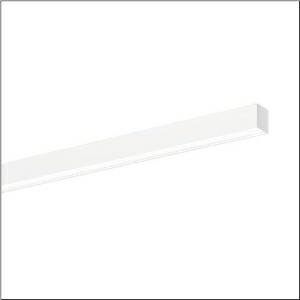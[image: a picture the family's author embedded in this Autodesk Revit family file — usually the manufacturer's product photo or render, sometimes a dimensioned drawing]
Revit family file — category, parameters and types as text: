
# Revit family: silica_21_51mx23dc4awb
name_source: partatom
category: Lighting Fixtures
units: mm (PartAtom-declared; Revit-internal decimal feet)

## family parameters
Cut with Voids When Loaded = No
Host = Face
Light Source = No
Part Type = Normal
Room Calculation Point = No
Round Connector Dimension = Use Diameter
Shared = No

## types (1)
- --- (1 x LED, 8200 lm, 58.2 W, 4000K)
    Apparent Load = 58 VA
    CIE Flux Codes = 78 96 99 100 100
    Color Rendering = 80
    Color Temperature = 4000K
    Default Elevation = 1800 mm
    Description = Silica 21, office luminaire, primary optical cover: prismatic diffuser, of PMMA, CAT 2 (L<= 3000cd/m²), light emission: direct distribution, primary light characteristic: symmetric, installation type: surface-mounted, LED, rated luminous flux: 8.200lm, luminous efficacy: 141lm/W, light colour: 840, colour temperature: 4000K, control gear: DALI 2, with terminal, 3+2-pole, max. 2.5mm², mains connection: 220..240V, AC, 50/60Hz, rated input power: 58.2W, luminaire housing, of aluminium, traffic white (RAL 9016), length: 3.004mm, width: 53mm, height: 53mm, protection rating (complete): IP20, insulation class (complete): insulation class I (protective earthing), certification: CE, permissible operating ambient temperature: 0..+35°C, standard: EN 50419, packaging unit: 1 piece
    Height = 53 mm
    Lamp = 1 x LED
    Lamp Light Flux = 8200 lm
    Lamp Power = 58.2 W
    Lamp count = 1
    Length = 3004 mm
    Luminous efficacy = 141 lm/W
    Manufacturer = Siteco
    ModVariant = No
    Model = 51MX23DC4AWB
    Mounting Place = Ceiling
    Mounting Type = Surface mounted
    Number of Poles = 1
    OnlyDefault = Yes
    Power Factor = 1
    Product Name = Silica 21
    Product group = office luminaire | ceiling mounted
    ProductGroupID = 301
    Protection Class = Protection class I
    Protection Degree = IP 20
    RLX_Detail_Level = 1
    RLX_Emergency_Light_Flux = 0 lm
    RLX_Emergency_Type = 0
    RLX_Emergency_Type_DB = No
    RlxData = <blob elided: 18713 chars, md5=0a9b26bc>
    Socket = socket
    Standby Power = 0 W
    System Light Flux = 8200 lm
    System Power = 58 W
    Type Comments = factory setting: luminous flux: 100 % | dim-lin: 254 | 323 mA
    Type Image = l_1335877.jpg
    URL = http://relux.com
    VarID = @adj_119673
    Voltage = 0 V
    Weight = 0.00 kg
    Width = 53 mm

## geometry (parser evidence)
native form markers: Blend x4, Sweep x10
no freeform markers — native parametric forms only
